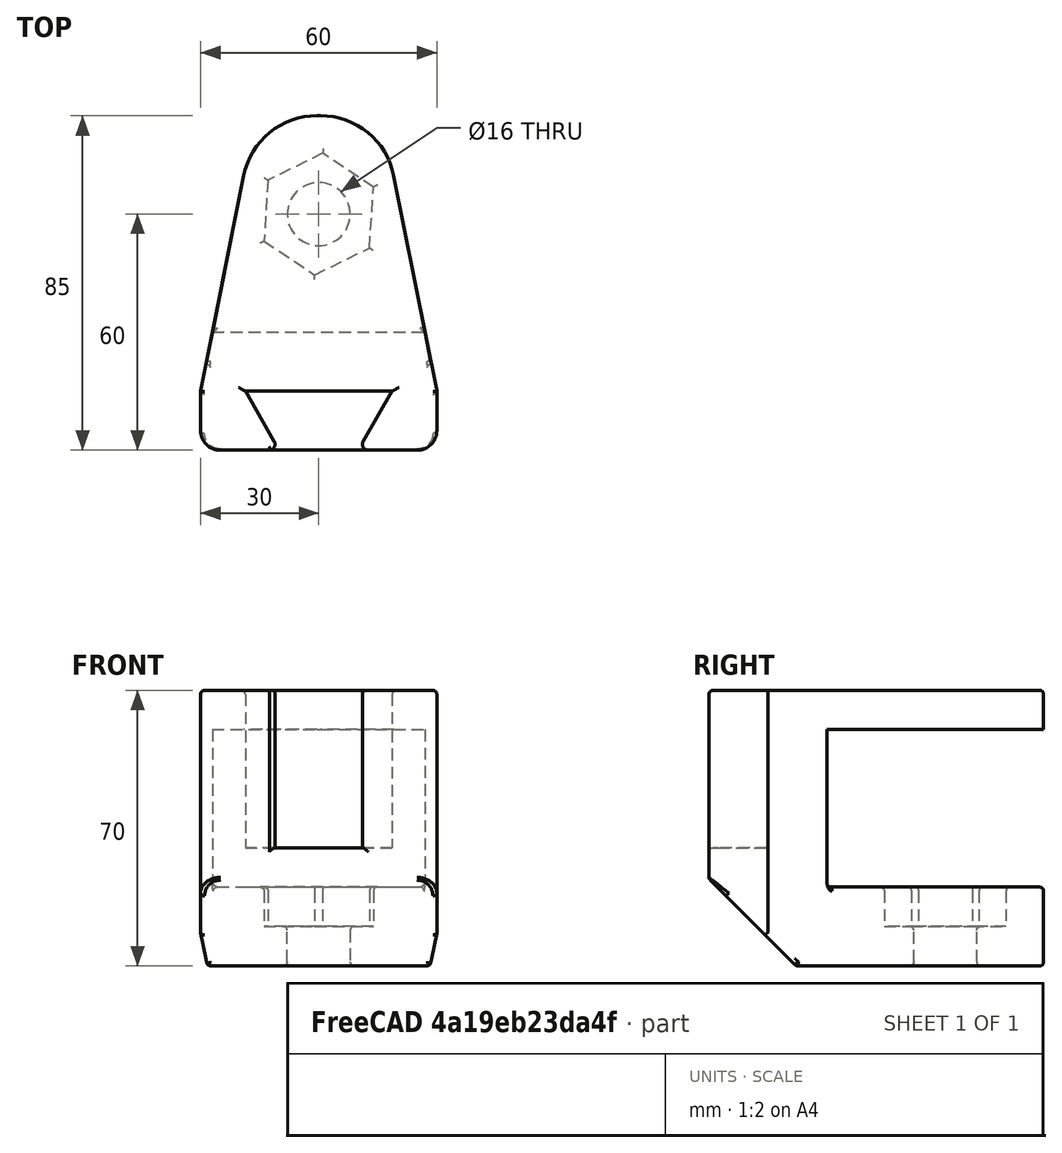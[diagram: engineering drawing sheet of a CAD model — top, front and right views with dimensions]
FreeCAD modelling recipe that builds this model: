
FCSTD DOCUMENT  (FreeCAD 1.0R39319 (Git))
Label: desk-clamp-base
License: All rights reserved
LicenseURL: https://en.wikipedia.org/wiki/All_rights_reserved
objects: Sketcher::SketchObject×14, PartDesign::Fillet×11, PartDesign::Plane×8, PartDesign::Pad×7, PartDesign::Pocket×7, PartDesign::Body×2
note: 113 computed .brp shape members not serialized (recipe doc carries the construction recipe); baked Part::Feature solids carry a one-line shape summary decoded from their .brp

FEATURE [Sketcher::SketchObject] Sketch
  ArcFitTolerance = 1e-06
  AttachmentSupport = -> [XY_Plane]
  FullyConstrained = false
  MakeInternals = false
  MapMode = 5
  sketch-geometry (8):
    g0: LineSegment StartX=-20 StartY=7.3e-15 StartZ=0 EndX=20 EndY=7.3e-15 EndZ=0
    g1: LineSegment StartX=20 StartY=7.3e-15 StartZ=0 EndX=20 EndY=50 EndZ=0
    g2: LineSegment StartX=1.4e-15 StartY=70 StartZ=0 EndX=-2.5983e-12 EndY=70 EndZ=0
    g3: LineSegment StartX=-20 StartY=50 StartZ=0 EndX=-20 EndY=7.1e-15 EndZ=0
    g4: ArcOfCircle CenterX=-2.64e-14 CenterY=50 CenterZ=0 NormalX=0 NormalY=0 NormalZ=1 AngleXU=0 Radius=20 StartAngle=1.5708 EndAngle=3.14159
    g5: GeomPoint [constr] X=-20 Y=70 Z=0
    g6: ArcOfCircle CenterX=1e-16 CenterY=50 CenterZ=0 NormalX=0 NormalY=0 NormalZ=1 AngleXU=0 Radius=20 StartAngle=7.3e-15 EndAngle=1.5708
    g7: GeomPoint [constr] X=20 Y=70 Z=0
  constraints (11):
    c: Coincident(g0,g1)
    c: Coincident(g3,g0)
    c: Horizontal(g0)
    c: Horizontal(g2)
    c: PointOnObject(g0,g-1)
    c: DistanceY(g0,g5) = 70
    c: DistanceX(g-1,g0) = 20
    c: PointOnObject(g5,g2)
    c: Tangent(g3,g4) = -1.5708
    c: PointOnObject(g7,g2)
    c: Tangent(g2,g6) = -1.5708
FEATURE [PartDesign::Pad] Pad
  Direction = (0,0,1)
  Length = 15
  Length2 = 10
  Profile = -> Sketch
  ReferenceAxis = -> Sketch [N_Axis]
  Refine = true
  Reversed = true
  Suppressed = false
  Type = 0
FEATURE [PartDesign::Plane] DatumPlane
  AttachmentSupport = -> [Pad]
  Length = 63.0767
  MapMode = 5
  Placement = pos=(0,0,-15) rot=(1,0,0;3.14159rad)
  ResizeMode = 0
  Width = 98.5767
FEATURE [Sketcher::SketchObject] Sketch001
  ArcFitTolerance = 1e-06
  AttachmentSupport = -> [DatumPlane]
  FullyConstrained = true
  MakeInternals = false
  MapMode = 5
  Placement = pos=(0,0,-15) rot=(1,0,0;3.14159rad)
  sketch-geometry (4):
    g0: LineSegment StartX=-20 StartY=0 StartZ=0 EndX=-20 EndY=-15 EndZ=0
    g1: LineSegment StartX=-20 StartY=-15 StartZ=0 EndX=20 EndY=-15 EndZ=0
    g2: LineSegment StartX=20 StartY=-15 StartZ=0 EndX=20 EndY=0 EndZ=0
    g3: LineSegment StartX=20 StartY=0 StartZ=0 EndX=-20 EndY=0 EndZ=0
  constraints (12):
    c: Coincident(g0,g1)
    c: Coincident(g1,g2)
    c: Coincident(g2,g3)
    c: Coincident(g3,g0)
    c: Vertical(g0)
    c: Vertical(g2)
    c: Horizontal(g1)
    c: Horizontal(g3)
    c: Distance(g0,g2) = 40
    c: Distance(g1,g3) = 15
    c: PointOnObject(g0,g-1)
    c: DistanceX(g0,g-1) = 20
FEATURE [PartDesign::Pad] Pad001
  BaseFeature = -> Pad
  Direction = (0,0,-1)
  Length = 40
  Length2 = 10
  Profile = -> Sketch001
  ReferenceAxis = -> Sketch001 [N_Axis]
  Refine = true
  Suppressed = false
  Type = 0
FEATURE [PartDesign::Plane] DatumPlane001
  AttachmentSupport = -> [Pad001]
  Length = 63.0767
  MapMode = 5
  Placement = pos=(0,0,-55) rot=(1,0,0;3.14159rad)
  ResizeMode = 0
  Width = 98.5767
FEATURE [Sketcher::SketchObject] Sketch002
  ArcFitTolerance = 1e-06
  AttachmentSupport = -> [DatumPlane001]
  FullyConstrained = false
  MakeInternals = false
  MapMode = 5
  Placement = pos=(0,0,-55) rot=(1,0,0;3.14159rad)
  sketch-geometry (8):
    g0: LineSegment StartX=-20 StartY=-6.3e-15 StartZ=0 EndX=-20 EndY=-50 EndZ=0
    g1: LineSegment StartX=-2.2859e-12 StartY=-70 StartZ=0 EndX=-9.09e-14 EndY=-70 EndZ=0
    g2: LineSegment StartX=20 StartY=-50 StartZ=0 EndX=20 EndY=-7.1e-15 EndZ=0
    g3: LineSegment StartX=20 StartY=-6.3e-15 StartZ=0 EndX=-20 EndY=-6.3e-15 EndZ=0
    g4: ArcOfCircle CenterX=-3.07e-14 CenterY=-50 CenterZ=0 NormalX=0 NormalY=0 NormalZ=1 AngleXU=0 Radius=20 StartAngle=3.14159 EndAngle=4.71239
    g5: GeomPoint [constr] X=-20 Y=-70 Z=0
    g6: ArcOfCircle CenterX=-3.04e-14 CenterY=-50 CenterZ=0 NormalX=0 NormalY=0 NormalZ=1 AngleXU=0 Radius=20 StartAngle=4.71239 EndAngle=6.28319
    g7: GeomPoint [constr] X=20 Y=-70 Z=0
  constraints (2):
    c: Tangent(g1,g6) = -1.5708
    c: Radius(g4) = 20
FEATURE [PartDesign::Pad] Pad002
  BaseFeature = -> Pad001
  Direction = (0,0,-1)
  Length = 25
  Length2 = 10
  Profile = -> Sketch002
  ReferenceAxis = -> Sketch002 [N_Axis]
  Refine = true
  Suppressed = false
  Type = 0
FEATURE [PartDesign::Plane] DatumPlane002
  AttachmentSupport = -> [Pad002]
  Length = 63.0767
  MapMode = 5
  Placement = pos=(0,0,-55) rot=(0,0,1;0rad)
  ResizeMode = 0
  Width = 98.5767
FEATURE [Sketcher::SketchObject] Sketch003
  ArcFitTolerance = 1e-06
  AttachmentSupport = -> [DatumPlane002]
  FullyConstrained = false
  MakeInternals = false
  MapMode = 5
  Placement = pos=(0,0,-55) rot=(0,0,1;0rad)
  sketch-geometry (11):
    g0: LineSegment [constr] StartX=-20.431 StartY=0 StartZ=0 EndX=19.569 EndY=0 EndZ=0
    g1: LineSegment [constr] StartX=19.569 StartY=0 StartZ=0 EndX=19.569 EndY=70 EndZ=0
    g2: LineSegment [constr] StartX=19.569 StartY=70 StartZ=0 EndX=-20.431 EndY=70 EndZ=0
    g3: LineSegment [constr] StartX=-20.431 StartY=70 StartZ=0 EndX=-20.431 EndY=0 EndZ=0
    g4: LineSegment StartX=13.4234 StartY=52.75 StartZ=0 EndX=0 EndY=60.5 EndZ=0
    g5: LineSegment StartX=0 StartY=60.5 StartZ=0 EndX=-13.4234 EndY=52.75 EndZ=0
    g6: LineSegment StartX=-13.4234 StartY=52.75 StartZ=0 EndX=-13.4234 EndY=37.25 EndZ=0
    g7: LineSegment StartX=-13.4234 StartY=37.25 StartZ=0 EndX=-1.8e-15 EndY=29.5 EndZ=0
    g8: LineSegment StartX=-1.8e-15 StartY=29.5 StartZ=0 EndX=13.4234 EndY=37.25 EndZ=0
    g9: LineSegment StartX=13.4234 StartY=37.25 StartZ=0 EndX=13.4234 EndY=52.75 EndZ=0
    g10: Circle [constr] CenterX=0 CenterY=45 CenterZ=0 NormalX=0 NormalY=0 NormalZ=1 AngleXU=0 Radius=15.5
  constraints (28):
    c: Coincident(g0,g1)
    c: Coincident(g1,g2)
    c: Coincident(g2,g3)
    c: Coincident(g3,g0)
    c: Horizontal(g0)
    c: Horizontal(g2)
    c: Vertical(g1)
    c: Vertical(g3)
    c: Distance(g1,g3) = 40
    c: Distance(g0,g2) = 70
    c: PointOnObject(g0,g-1)
    c: Coincident(g4,g5)
    c: Coincident(g5,g6)
    c: Coincident(g6,g7)
    c: Coincident(g7,g8)
    c: Coincident(g8,g9)
    c: Coincident(g9,g4)
    c: Equal(g4, g5-g9) x5
    c: PointOnObject(g4,g10)
    c: PointOnObject(g5,g10)
    c: PointOnObject(g6,g10)
    c: PointOnObject(g7,g10)
    c: PointOnObject(g8,g10)
    c: PointOnObject(g9,g10)
    c: Radius(g10) = 15.5
    c: PointOnObject(g10,g-2)
    c: DistanceX(g10,g4) = 0
    c: DistanceY(g-1,g10) = 45
FEATURE [PartDesign::Pocket] Pocket
  BaseFeature = -> Pad002
  Direction = (0,0,-1)
  Length = 10
  Length2 = 5
  Profile = -> Sketch003
  ReferenceAxis = -> Sketch003 [N_Axis]
  Refine = true
  Suppressed = false
  Type = 0
FEATURE [PartDesign::Fillet] Fillet
  Base = -> Pocket [Edge33,Edge32,Edge31,Edge30,Edge29,Edge34]
  BaseFeature = -> Pocket
  Radius = 1
  Refine = true
  SupportTransform = false
  Suppressed = false
  UseAllEdges = false
FEATURE [Sketcher::SketchObject] Sketch004
  ArcFitTolerance = 1e-06
  AttachmentSupport = -> [DatumPlane002]
  FullyConstrained = false
  MakeInternals = false
  MapMode = 5
  Placement = pos=(0,0,-55) rot=(0,0,1;0rad)
  sketch-geometry (1):
    g0: Circle CenterX=0 CenterY=45.4965 CenterZ=0 NormalX=0 NormalY=0 NormalZ=1 AngleXU=0 Radius=10
  constraints (2):
    c: Diameter(g0) = 20
    c: PointOnObject(g0,g-2)
FEATURE [PartDesign::Pocket] Pocket001
  BaseFeature = -> Fillet
  Direction = (0,0,-1)
  Length = 40
  Length2 = 5
  Profile = -> Sketch004
  ReferenceAxis = -> Sketch004 [N_Axis]
  Refine = true
  Suppressed = false
  Type = 0
FEATURE [PartDesign::Fillet] Fillet001
  Base = -> Pocket001 [Edge60,Edge58]
  BaseFeature = -> Pocket001
  Radius = 1
  Refine = true
  SupportTransform = false
  Suppressed = false
  UseAllEdges = false
FEATURE [PartDesign::Fillet] Fillet003
  Base = -> Fillet001 [Face12]
  BaseFeature = -> Fillet001
  Radius = 1
  Refine = true
  SupportTransform = false
  Suppressed = false
  UseAllEdges = false
FEATURE [PartDesign::Plane] DatumPlane003
  AttachmentSupport = -> [Fillet003]
  Length = 63.0767
  MapMode = 5
  ResizeMode = 0
  Width = 98.5767
FEATURE [Sketcher::SketchObject] Sketch005
  ArcFitTolerance = 1e-06
  AttachmentSupport = -> [DatumPlane003]
  FullyConstrained = false
  MakeInternals = false
  MapMode = 5
  sketch-geometry (19):
    g0: LineSegment StartX=-20 StartY=15 StartZ=0 EndX=20 EndY=15 EndZ=0
    g1: LineSegment StartX=28.6609 StartY=0 StartZ=0 EndX=28.6609 EndY=-10 EndZ=0
    g2: LineSegment StartX=23.6609 StartY=-15 StartZ=0 EndX=11.7321 EndY=-15 EndZ=0
    g3: LineSegment StartX=10.8661 StartY=-13.5 StartZ=0 EndX=18.6609 EndY=-7.24726e-05 EndZ=0
    g4: LineSegment StartX=18.6609 StartY=-7.24726e-05 StartZ=0 EndX=-18.6607 EndY=-7.24726e-05 EndZ=0
    g5: LineSegment StartX=-18.6607 StartY=-7.24726e-05 StartZ=0 EndX=-10.8661 EndY=-13.5 EndZ=0
    g6: LineSegment StartX=-11.7321 StartY=-15 StartZ=0 EndX=-23.6602 EndY=-15 EndZ=0
    g7: LineSegment StartX=-28.6602 StartY=-10 StartZ=0 EndX=-28.6602 EndY=0 EndZ=0
    g8: GeomPoint [constr] X=28.6609 Y=0 Z=0
    g9: ArcOfCircle CenterX=-23.6602 CenterY=-10 CenterZ=0 NormalX=0 NormalY=0 NormalZ=1 AngleXU=0 Radius=5 StartAngle=3.14159 EndAngle=4.71239
    g10: GeomPoint [constr] X=-28.6602 Y=-15 Z=0
    g11: ArcOfCircle CenterX=23.6609 CenterY=-10 CenterZ=0 NormalX=0 NormalY=0 NormalZ=1 AngleXU=0 Radius=5 StartAngle=4.71239 EndAngle=6.28319
    g12: GeomPoint [constr] X=28.6609 Y=-15 Z=0
    g13: LineSegment StartX=-28.6602 StartY=0 StartZ=0 EndX=-20 EndY=15 EndZ=0
    g14: LineSegment StartX=20 StartY=15 StartZ=0 EndX=28.6609 EndY=0 EndZ=0
    g15: ArcOfCircle CenterX=11.7321 CenterY=-14 CenterZ=0 NormalX=0 NormalY=0 NormalZ=1 AngleXU=0 Radius=1 StartAngle=2.61796 EndAngle=4.71239
    g16: GeomPoint [constr] X=10 Y=-15 Z=0
    g17: ArcOfCircle CenterX=-11.7321 CenterY=-14 CenterZ=0 NormalX=0 NormalY=0 NormalZ=1 AngleXU=0 Radius=1 StartAngle=4.71239 EndAngle=6.80681
    g18: GeomPoint [constr] X=-10 Y=-15 Z=0
  constraints (42):
    c: Coincident(g3,g4)
    c: Coincident(g4,g5)
    c: Parallel(g0,g-1)
    c: Parallel(g2,g-1)
    c: Parallel(g4,g-1)
    c: Parallel(g6,g-1)
    c: Parallel(g1,g-2)
    c: Parallel(g-2,g7)
    c: DistanceY(g8,g-1) = 0
    c: DistanceY(g18,g-1) = 15
    c: DistanceY(g16,g-1) = 15
    c: DistanceX(g18,g-1) = 10
    c: DistanceX(g-1,g16) = 10
    c: DistanceX(g3,g8) = 10
    c: PointOnObject(g8,g1)
    c: PointOnObject(g10,g6)
    c: PointOnObject(g10,g7)
    c: Tangent(g6,g9) = 1.5708
    c: Tangent(g7,g9) = 1.5708
    c: PointOnObject(g12,g1)
    c: PointOnObject(g12,g2)
    c: Tangent(g1,g11) = 1.5708
    c: Tangent(g2,g11) = 1.5708
    c: Radius(g11) = 5
    c: Radius(g9) = 5
    c: DistanceY(g-1,g0) = 15
    c: DistanceY(g1,g-1) = 0
    c: DistanceY(g7,g-1) = 0
    c: Coincident(g13,g7)
    c: Coincident(g13,g0)
    c: Coincident(g14,g0)
    c: Coincident(g14,g1)
    c: PointOnObject(g16,g2)
    c: PointOnObject(g16,g3)
    c: Tangent(g2,g15) = 1.5708
    c: Tangent(g3,g15) = 1.5708
    c: PointOnObject(g18,g5)
    c: PointOnObject(g18,g6)
    c: Tangent(g5,g17) = 1.5708
    c: Tangent(g6,g17) = 1.5708
    c: Radius(g17) = 1
    c: Radius(g15) = 1
FEATURE [PartDesign::Pad] Pad003
  BaseFeature = -> Fillet003
  Direction = (0,0,1)
  Length = 55
  Length2 = 10
  Profile = -> Sketch005
  ReferenceAxis = -> Sketch005 [N_Axis]
  Refine = true
  Reversed = true
  Suppressed = false
  Type = 0
FEATURE [PartDesign::Plane] DatumPlane004
  AttachmentOffset = pos=(0,0,-55) rot=(0,0,1;0rad)
  Length = 63.0767
  MapMode = 5
  Placement = pos=(0,0,-55) rot=(0,0,1;0rad)
  ResizeMode = 0
  Width = 98.5767
FEATURE [Sketcher::SketchObject] Sketch006
  ArcFitTolerance = 1e-06
  AttachmentSupport = -> [DatumPlane004]
  FullyConstrained = false
  MakeInternals = false
  MapMode = 5
  Placement = pos=(0,0,-55) rot=(0,0,1;0rad)
  sketch-geometry (13):
    g0: LineSegment StartX=-20 StartY=15 StartZ=0 EndX=20 EndY=15 EndZ=0
    g1: LineSegment StartX=28.6602 StartY=0 StartZ=0 EndX=28.6602 EndY=-10 EndZ=0
    g2: LineSegment StartX=23.6602 StartY=-15 StartZ=0 EndX=10 EndY=-15 EndZ=0
    g3: LineSegment StartX=-10 StartY=-15 StartZ=0 EndX=-23.6603 EndY=-15 EndZ=0
    g4: LineSegment StartX=-28.6603 StartY=-10 StartZ=0 EndX=-28.6603 EndY=0 EndZ=0
    g5: GeomPoint [constr] X=28.6602 Y=0 Z=0
    g6: ArcOfCircle CenterX=-23.6603 CenterY=-10 CenterZ=0 NormalX=0 NormalY=0 NormalZ=1 AngleXU=0 Radius=5 StartAngle=3.14159 EndAngle=4.71239
    g7: GeomPoint [constr] X=-28.6603 Y=-15 Z=0
    g8: ArcOfCircle CenterX=23.6602 CenterY=-10 CenterZ=0 NormalX=0 NormalY=0 NormalZ=1 AngleXU=0 Radius=5 StartAngle=4.71239 EndAngle=6.28319
    g9: GeomPoint [constr] X=28.6602 Y=-15 Z=0
    g10: LineSegment StartX=-28.6603 StartY=0 StartZ=0 EndX=-20 EndY=15 EndZ=0
    g11: LineSegment StartX=20 StartY=15 StartZ=0 EndX=28.6602 EndY=0 EndZ=0
    g12: LineSegment StartX=-10 StartY=-15 StartZ=0 EndX=10 EndY=-15 EndZ=0
  constraints (30):
    c: Parallel(g0,g-1)
    c: Parallel(g2,g-1)
    c: Parallel(g3,g-1)
    c: Parallel(g1,g-2)
    c: Parallel(g-2,g4)
    c: DistanceY(g5,g-1) = 0
    c: DistanceY(g3,g-1) = 15
    c: DistanceY(g2,g-1) = 15
    c: DistanceX(g3,g-1) = 10
    c: DistanceX(g-1,g2) = 10
    c: PointOnObject(g5,g1)
    c: PointOnObject(g7,g3)
    c: PointOnObject(g7,g4)
    c: Tangent(g3,g6) = 1.5708
    c: Tangent(g4,g6) = 1.5708
    c: PointOnObject(g9,g1)
    c: PointOnObject(g9,g2)
    c: Tangent(g1,g8) = 1.5708
    c: Tangent(g2,g8) = 1.5708
    c: Radius(g8) = 5
    c: Radius(g6) = 5
    c: DistanceY(g-1,g0) = 15
    c: DistanceY(g1,g-1) = 0
    c: DistanceY(g4,g-1) = 0
    c: Coincident(g10,g4)
    c: Coincident(g10,g0)
    c: Coincident(g11,g0)
    c: Coincident(g11,g1)
    c: Coincident(g12,g3)
    c: Coincident(g12,g2)
FEATURE [PartDesign::Pad] Pad004
  BaseFeature = -> Pad003
  Direction = (0,0,1)
  Length = 25
  Length2 = 10
  Profile = -> Sketch006
  ReferenceAxis = -> Sketch006 [N_Axis]
  Refine = true
  Reversed = true
  Suppressed = false
  Type = 0
FEATURE [PartDesign::Fillet] Fillet007
  Base = -> Pad004 [Edge88]
  BaseFeature = -> Pad004
  Radius = 1
  Refine = true
  SupportTransform = false
  Suppressed = false
  UseAllEdges = false
FEATURE [PartDesign::Plane] DatumPlane005
  AttachmentSupport = -> [Fillet007]
  Length = 63.0767
  MapMode = 5
  Placement = pos=(0,0,-55) rot=(0,0,1;0rad)
  ResizeMode = 0
  Width = 98.5767
FEATURE [Sketcher::SketchObject] Sketch007
  ArcFitTolerance = 1e-06
  AttachmentSupport = -> [DatumPlane005]
  FullyConstrained = false
  MakeInternals = false
  MapMode = 5
  Placement = pos=(0,0,-55) rot=(0,0,1;0rad)
  sketch-geometry (13):
    g0: LineSegment StartX=-20 StartY=15 StartZ=0 EndX=20 EndY=15 EndZ=0
    g1: LineSegment StartX=28.6602 StartY=0 StartZ=0 EndX=28.6602 EndY=-10 EndZ=0
    g2: LineSegment StartX=23.6602 StartY=-15 StartZ=0 EndX=10 EndY=-15 EndZ=0
    g3: LineSegment StartX=-10 StartY=-15 StartZ=0 EndX=-23.6603 EndY=-15 EndZ=0
    g4: LineSegment StartX=-28.6603 StartY=-10 StartZ=0 EndX=-28.6603 EndY=0 EndZ=0
    g5: GeomPoint [constr] X=28.6602 Y=0 Z=0
    g6: ArcOfCircle CenterX=-23.6603 CenterY=-10 CenterZ=0 NormalX=0 NormalY=0 NormalZ=1 AngleXU=0 Radius=5 StartAngle=3.14159 EndAngle=4.71239
    g7: GeomPoint [constr] X=-28.6603 Y=-15 Z=0
    g8: ArcOfCircle CenterX=23.6602 CenterY=-10 CenterZ=0 NormalX=0 NormalY=0 NormalZ=1 AngleXU=0 Radius=5 StartAngle=4.71239 EndAngle=6.28319
    g9: GeomPoint [constr] X=28.6602 Y=-15 Z=0
    g10: LineSegment StartX=-28.6603 StartY=0 StartZ=0 EndX=-20 EndY=15 EndZ=0
    g11: LineSegment StartX=20 StartY=15 StartZ=0 EndX=28.6602 EndY=0 EndZ=0
    g12: LineSegment StartX=-10 StartY=-15 StartZ=0 EndX=10 EndY=-15 EndZ=0
  constraints (30):
    c: Parallel(g0,g-1)
    c: Parallel(g2,g-1)
    c: Parallel(g3,g-1)
    c: Parallel(g1,g-2)
    c: Parallel(g-2,g4)
    c: DistanceY(g5,g-1) = 0
    c: DistanceY(g3,g-1) = 15
    c: DistanceY(g2,g-1) = 15
    c: DistanceX(g3,g-1) = 10
    c: DistanceX(g-1,g2) = 10
    c: PointOnObject(g5,g1)
    c: PointOnObject(g7,g3)
    c: PointOnObject(g7,g4)
    c: Tangent(g3,g6) = 1.5708
    c: Tangent(g4,g6) = 1.5708
    c: PointOnObject(g9,g1)
    c: PointOnObject(g9,g2)
    c: Tangent(g1,g8) = 1.5708
    c: Tangent(g2,g8) = 1.5708
    c: Radius(g8) = 5
    c: Radius(g6) = 5
    c: DistanceY(g-1,g0) = 15
    c: DistanceY(g1,g-1) = 0
    c: DistanceY(g4,g-1) = 0
    c: Coincident(g10,g4)
    c: Coincident(g10,g0)
    c: Coincident(g11,g0)
    c: Coincident(g11,g1)
    c: Coincident(g12,g3)
    c: Coincident(g12,g2)
FEATURE [PartDesign::Pad] Pad005
  BaseFeature = -> Fillet007
  Direction = (0,0,1)
  Length = 15
  Length2 = 10
  Profile = -> Sketch007
  ReferenceAxis = -> Sketch007 [N_Axis]
  Refine = true
  Reversed = true
  Suppressed = false
  Type = 0
FEATURE [PartDesign::Fillet] Fillet008
  Base = -> Pad005 [Edge34]
  BaseFeature = -> Pad005
  Radius = 1
  Refine = true
  SupportTransform = false
  Suppressed = false
  UseAllEdges = false
FEATURE [PartDesign::Body] Body
  AllowCompound = false
  Group = -> [Sketch,Pad,DatumPlane,Sketch001,Pad001,DatumPlane001,Sketch002,Pad002,DatumPlane002,Sketch003,Pocket,Fillet,Sketch004,Pocket001,Fillet001,Fillet003,DatumPlane003,Sketch005,Pad003,DatumPlane004,Sketch006,Pad004,Fillet007,DatumPlane005,Sketch007,Pad005,Fillet008]
  Origin = -> Origin
  Tip = -> Fillet008
FEATURE [Sketcher::SketchObject] Sketch008
  ArcFitTolerance = 1e-06
  AttachmentSupport = -> [XY_Plane001]
  FullyConstrained = false
  MakeInternals = false
  MapMode = 5
  sketch-geometry (14):
    g0: LineSegment StartX=-30 StartY=-10 StartZ=0 EndX=-30 EndY=0.00573399 EndZ=0
    g1: LineSegment StartX=-30 StartY=0.00573399 StartZ=0 EndX=-19.055 EndY=54.7265 EndZ=0
    g2: LineSegment StartX=-0.423976 StartY=70 StartZ=0 EndX=0.423834 EndY=70 EndZ=0
    g3: LineSegment StartX=19.0548 StartY=54.7263 StartZ=0 EndX=30 EndY=0.00248185 EndZ=0
    g4: LineSegment StartX=30 StartY=0.00248185 StartZ=0 EndX=30 EndY=-10 EndZ=0
    g5: LineSegment StartX=25 StartY=-15 StartZ=0 EndX=10 EndY=-15 EndZ=0
    g6: ArcOfCircle CenterX=0.423834 CenterY=51 CenterZ=0 NormalX=0 NormalY=0 NormalZ=1 AngleXU=0 Radius=19 StartAngle=0.197402 EndAngle=1.5708
    g7: GeomPoint [constr] X=16 Y=70 Z=0
    g8: ArcOfCircle CenterX=-0.423976 CenterY=51 CenterZ=0 NormalX=0 NormalY=0 NormalZ=1 AngleXU=0 Radius=19 StartAngle=1.5708 EndAngle=2.94418
    g9: GeomPoint [constr] X=-16 Y=70 Z=0
    g10: ArcOfCircle CenterX=-25 CenterY=-10 CenterZ=0 NormalX=0 NormalY=0 NormalZ=1 AngleXU=0 Radius=5 StartAngle=3.14159 EndAngle=4.71239
    g11: ArcOfCircle CenterX=25 CenterY=-10 CenterZ=0 NormalX=0 NormalY=0 NormalZ=1 AngleXU=0 Radius=5 StartAngle=4.71239 EndAngle=6.28319
    g12: LineSegment StartX=-10 StartY=-15 StartZ=0 EndX=-25 EndY=-15 EndZ=0
    g13: LineSegment StartX=-10 StartY=-15 StartZ=0 EndX=10 EndY=-15 EndZ=0
  constraints (33):
    c: Coincident(g0,g1)
    c: Coincident(g3,g4)
    c: Parallel(g5,g-1)
    c: Parallel(g2,g-1)
    c: Parallel(g4,g-2)
    c: Parallel(g0,g-2)
    c: DistanceY(g-1,g7) = 70
    c: DistanceX(g0,g-1) = 30
    c: DistanceX(g9,g-1) = 16
    c: DistanceX(g-1,g7) = 16
    c: PointOnObject(g7,g2)
    c: PointOnObject(g7,g3)
    c: Tangent(g2,g6) = 1.5708
    c: Tangent(g3,g6) = 1.5708
    c: PointOnObject(g9,g1)
    c: PointOnObject(g9,g2)
    c: Tangent(g1,g8) = 1.5708
    c: Tangent(g2,g8) = 1.5708
    c: Tangent(g0,g10) = 1.5708
    c: Coincident(g12,g10) = 1.5708
    c: Tangent(g4,g11) = 1.5708
    c: Tangent(g5,g11) = 1.5708
    c: Radius(g11) = 5
    c: Radius(g10) = 5
    c: Radius(g8) = 19
    c: Radius(g6) = 19
    c: PointOnObject(g13,g12)
    c: Parallel(g12,g-1)
    c: DistanceY(g13,g-1) = 15
    c: DistanceY(g5,g-1) = 15
    c: DistanceX(g13,g-1) = 10
    c: DistanceX(g-1,g5) = 10
    c: Coincident(g13,g5)
FEATURE [PartDesign::Pad] Pad006
  Direction = (0,0,1)
  Length = 70
  Length2 = 10
  Profile = -> Sketch008
  ReferenceAxis = -> Sketch008 [N_Axis]
  Refine = true
  Reversed = true
  Suppressed = false
  Type = 0
FEATURE [Sketcher::SketchObject] Sketch009
  ArcFitTolerance = 1e-06
  AttachmentOffset = pos=(0,0,-10) rot=(0,0,1;0rad)
  AttachmentSupport = -> [XY_Plane001]
  FullyConstrained = false
  MakeInternals = false
  MapMode = 5
  Placement = pos=(0,0,-10) rot=(0,0,1;0rad)
  sketch-geometry (8):
    g0: LineSegment StartX=-27.0009 StartY=15 StartZ=0 EndX=-19.055 EndY=54.7265 EndZ=0
    g1: LineSegment StartX=-0.423976 StartY=70 StartZ=0 EndX=0.423834 EndY=70 EndZ=0
    g2: LineSegment StartX=19.0548 StartY=54.7263 StartZ=0 EndX=27.0004 EndY=15 EndZ=0
    g3: ArcOfCircle CenterX=0.423834 CenterY=51 CenterZ=0 NormalX=0 NormalY=0 NormalZ=1 AngleXU=0 Radius=19 StartAngle=0.197402 EndAngle=1.5708
    g4: GeomPoint [constr] X=16 Y=70 Z=0
    g5: ArcOfCircle CenterX=-0.423976 CenterY=51 CenterZ=0 NormalX=0 NormalY=0 NormalZ=1 AngleXU=0 Radius=19 StartAngle=1.5708 EndAngle=2.94418
    g6: GeomPoint [constr] X=-16 Y=70 Z=0
    g7: LineSegment StartX=-27.0009 StartY=15 StartZ=0 EndX=27.0004 EndY=15 EndZ=0
  constraints (17):
    c: Parallel(g1,g-1)
    c: DistanceY(g-1,g4) = 70
    c: DistanceX(g6,g-1) = 16
    c: DistanceX(g-1,g4) = 16
    c: PointOnObject(g4,g1)
    c: PointOnObject(g4,g2)
    c: Tangent(g1,g3) = 1.5708
    c: Tangent(g2,g3) = 1.5708
    c: PointOnObject(g6,g0)
    c: PointOnObject(g6,g1)
    c: Tangent(g0,g5) = 1.5708
    c: Tangent(g1,g5) = 1.5708
    c: Radius(g5) = 19
    c: Radius(g3) = 19
    c: Horizontal(g7)
    c: Coincident(g7,g0)
    c: Coincident(g2,g7)
FEATURE [PartDesign::Pocket] Pocket002
  BaseFeature = -> Pad006
  Direction = (0,0,-1)
  Length = 40
  Length2 = 5
  Profile = -> Sketch009
  ReferenceAxis = -> Sketch009 [N_Axis]
  Refine = true
  Suppressed = false
  Type = 0
FEATURE [PartDesign::Plane] DatumPlane006
  AttachmentSupport = -> [Pocket002]
  Length = 75.0997
  MapMode = 5
  Placement = pos=(0,0,-50) rot=(0,0,1;0rad)
  ResizeMode = 0
  Width = 110.1
FEATURE [Sketcher::SketchObject] Sketch011
  ArcFitTolerance = 1e-06
  AttachmentSupport = -> [DatumPlane006]
  FullyConstrained = true
  MakeInternals = false
  MapMode = 5
  Placement = pos=(0,0,-50) rot=(0,0,1;0rad)
  sketch-geometry (1):
    g0: Circle CenterX=0 CenterY=45 CenterZ=0 NormalX=0 NormalY=0 NormalZ=1 AngleXU=0 Radius=8
  constraints (3):
    c: Diameter(g0) = 16
    c: PointOnObject(g0,g-2)
    c: DistanceY(g-1,g0) = 45
FEATURE [PartDesign::Pocket] Pocket003
  BaseFeature = -> Pocket002
  Direction = (0,0,-1)
  Length = 20
  Length2 = 5
  Profile = -> Sketch011
  ReferenceAxis = -> Sketch011 [N_Axis]
  Refine = true
  Suppressed = false
  Type = 0
FEATURE [Sketcher::SketchObject] Sketch012
  ArcFitTolerance = 1e-06
  AttachmentSupport = -> [DatumPlane006]
  FullyConstrained = false
  MakeInternals = false
  MapMode = 5
  Placement = pos=(0,0,-50) rot=(0,0,1;0rad)
  sketch-geometry (7):
    g0: LineSegment StartX=13.9057 StartY=51.847 StartZ=0 EndX=1.02316 EndY=60.4662 EndZ=0
    g1: LineSegment StartX=1.02316 StartY=60.4662 StartZ=0 EndX=-12.8825 EndY=53.6192 EndZ=0
    g2: LineSegment StartX=-12.8825 StartY=53.6192 StartZ=0 EndX=-13.9057 EndY=38.153 EndZ=0
    g3: LineSegment StartX=-13.9057 StartY=38.153 StartZ=0 EndX=-1.02316 EndY=29.5338 EndZ=0
    g4: LineSegment StartX=-1.02316 StartY=29.5338 StartZ=0 EndX=12.8825 EndY=36.3808 EndZ=0
    g5: LineSegment StartX=12.8825 StartY=36.3808 StartZ=0 EndX=13.9057 EndY=51.847 EndZ=0
    g6: Circle [constr] CenterX=0 CenterY=45 CenterZ=0 NormalX=0 NormalY=0 NormalZ=1 AngleXU=0 Radius=15.5
  constraints (16):
    c: Coincident(g0,g1)
    c: Coincident(g1,g2)
    c: Coincident(g2,g3)
    c: Coincident(g3,g4)
    c: Coincident(g4,g5)
    c: Coincident(g5,g0)
    c: Equal(g0, g1-g5) x5
    c: PointOnObject(g0,g6)
    c: PointOnObject(g1,g6)
    c: PointOnObject(g2,g6)
    c: PointOnObject(g3,g6)
    c: PointOnObject(g4,g6)
    c: PointOnObject(g5,g6)
    c: Radius(g6) = 15.5
    c: PointOnObject(g6,g-2)
    c: DistanceY(g-1,g6) = 45
FEATURE [PartDesign::Pocket] Pocket004
  BaseFeature = -> Pocket003
  Direction = (0,0,-1)
  Length = 10
  Length2 = 5
  Profile = -> Sketch012
  ReferenceAxis = -> Sketch012 [N_Axis]
  Refine = true
  Suppressed = false
  Type = 0
FEATURE [Sketcher::SketchObject] Sketch013
  ArcFitTolerance = 1e-06
  AttachmentSupport = -> [XY_Plane001]
  FullyConstrained = false
  MakeInternals = false
  MapMode = 5
  sketch-geometry (8):
    g0: LineSegment StartX=-11.294 StartY=-12.7529 StartZ=0 EndX=-18.6492 EndY=-0.0132244 EndZ=0
    g1: LineSegment StartX=-18.6492 StartY=-0.0132244 StartZ=0 EndX=18.6526 EndY=-0.0132244 EndZ=0
    g2: LineSegment StartX=18.6526 StartY=-0.0132244 StartZ=0 EndX=11.299 EndY=-12.75 EndZ=0
    g3: LineSegment [constr] StartX=10 StartY=-15 StartZ=0 EndX=22.5038 EndY=-7.78093 EndZ=0
    g4: LineSegment [constr] StartX=-10 StartY=-15 StartZ=0 EndX=-16.855 EndY=-11.0422 EndZ=0
    g5: ArcOfCircle CenterX=12.5981 CenterY=-13.5 CenterZ=0 NormalX=0 NormalY=0 NormalZ=1 AngleXU=0 Radius=1.5 StartAngle=2.61799 EndAngle=4.71239
    g6: ArcOfCircle CenterX=-12.593 CenterY=-13.5029 CenterZ=0 NormalX=0 NormalY=0 NormalZ=1 AngleXU=0 Radius=1.5 StartAngle=4.7747 EndAngle=6.80678
    g7: LineSegment StartX=12.5981 StartY=-15 StartZ=0 EndX=-12.4996 EndY=-15 EndZ=0
  constraints (20):
    c: Coincident(g0,g1)
    c: Horizontal(g1)
    c: Coincident(g1,g2)
    c: DistanceY(g4,g-1) = 15
    c: DistanceY(g3,g-1) = 15
    c: DistanceX(g4,g-1) = 10
    c: DistanceX(g-1,g3) = 10
    c: Angle(g0,g-1) = 1.0472
    c: Angle(g-1,g2) = 1.0472
    c: Angle(g3,g2) = 0.523599
    c: Angle(g0,g4) = 0.523599
    c: PointOnObject(g5,g3)
    c: PointOnObject(g6,g4)
    c: Diameter(g5) = 3
    c: Diameter(g6) = 3
    c: Horizontal(g7)
    c: Tangent(g6,g0) = -1.5708
    c: Coincident(g6,g7)
    c: Tangent(g5,g2) = -1.5708
    c: Tangent(g5,g7) = 1.5708
FEATURE [PartDesign::Pocket] Pocket005
  BaseFeature = -> Pocket004
  Direction = (0,0,-1)
  Length = 40
  Length2 = 5
  Profile = -> Sketch013
  ReferenceAxis = -> Sketch013 [N_Axis]
  Refine = true
  Suppressed = false
  Type = 0
FEATURE [PartDesign::Fillet] Fillet009
  Base = -> Pocket005 [Face4]
  BaseFeature = -> Pocket005
  Radius = 1
  Refine = true
  SupportTransform = false
  Suppressed = false
  UseAllEdges = false
FEATURE [PartDesign::Fillet] Fillet010
  Base = -> Fillet009 [Face4]
  BaseFeature = -> Fillet009
  Radius = 1
  Refine = true
  SupportTransform = false
  Suppressed = false
  UseAllEdges = false
FEATURE [PartDesign::Fillet] Fillet011
  Base = -> Fillet010 [Face15]
  BaseFeature = -> Fillet010
  Radius = 1
  Refine = true
  SupportTransform = false
  Suppressed = false
  UseAllEdges = false
FEATURE [PartDesign::Fillet] Fillet012
  Base = -> Fillet011 [Edge162]
  BaseFeature = -> Fillet011
  Radius = 1
  Refine = true
  SupportTransform = false
  Suppressed = false
  UseAllEdges = false
FEATURE [PartDesign::Fillet] Fillet013
  Base = -> Fillet012 [Edge86]
  BaseFeature = -> Fillet012
  Radius = 1
  Refine = true
  SupportTransform = false
  Suppressed = false
  UseAllEdges = false
FEATURE [PartDesign::Plane] DatumPlane007
  AttachmentOffset = pos=(0,0,0) rot=(-1,0,0;0.785398rad)
  AttachmentSupport = -> [Fillet013]
  Length = 77.9566
  MapMode = 5
  Placement = pos=(0,0,-70) rot=(1,0,0;2.35619rad)
  ResizeMode = 0
  Width = 152.307
FEATURE [Sketcher::SketchObject] Sketch014
  ArcFitTolerance = 1e-06
  AttachmentSupport = -> [DatumPlane007]
  FullyConstrained = false
  MakeInternals = false
  MapMode = 5
  Placement = pos=(0,0,-70) rot=(1,0,0;2.35619rad)
  sketch-geometry (4):
    g0: LineSegment StartX=-41.964 StartY=40.5039 StartZ=0 EndX=-41.964 EndY=-35.1261 EndZ=0
    g1: LineSegment StartX=-41.964 StartY=-35.1261 StartZ=0 EndX=41.3109 EndY=-35.1261 EndZ=0
    g2: LineSegment StartX=41.3109 StartY=-35.1261 StartZ=0 EndX=41.3109 EndY=40.5039 EndZ=0
    g3: LineSegment StartX=41.3109 StartY=40.5039 StartZ=0 EndX=-41.964 EndY=40.5039 EndZ=0
  constraints (8):
    c: Coincident(g0,g1)
    c: Coincident(g1,g2)
    c: Coincident(g2,g3)
    c: Coincident(g3,g0)
    c: Vertical(g0)
    c: Vertical(g2)
    c: Horizontal(g1)
    c: Horizontal(g3)
FEATURE [PartDesign::Pocket] Pocket006
  BaseFeature = -> Fillet013
  Direction = (0,0.707107,0.707107)
  Length = 5
  Length2 = 5
  Profile = -> Sketch014
  ReferenceAxis = -> Sketch014 [N_Axis]
  Refine = true
  Suppressed = false
  Type = 0
FEATURE [PartDesign::Fillet] Fillet014
  Base = -> Pocket006 [Face5]
  BaseFeature = -> Pocket006
  Radius = 1
  Refine = true
  SupportTransform = false
  Suppressed = false
  UseAllEdges = false
FEATURE [PartDesign::Body] Body001
  AllowCompound = false
  Group = -> [Sketch008,Pad006,Sketch009,Pocket002,DatumPlane006,Sketch011,Pocket003,Sketch012,Pocket004,Sketch013,Pocket005,Fillet009,Fillet010,Fillet011,Fillet012,Fillet013,DatumPlane007,Sketch014,Pocket006,Fillet014]
  Origin = -> Origin001
  Tip = -> Fillet014
